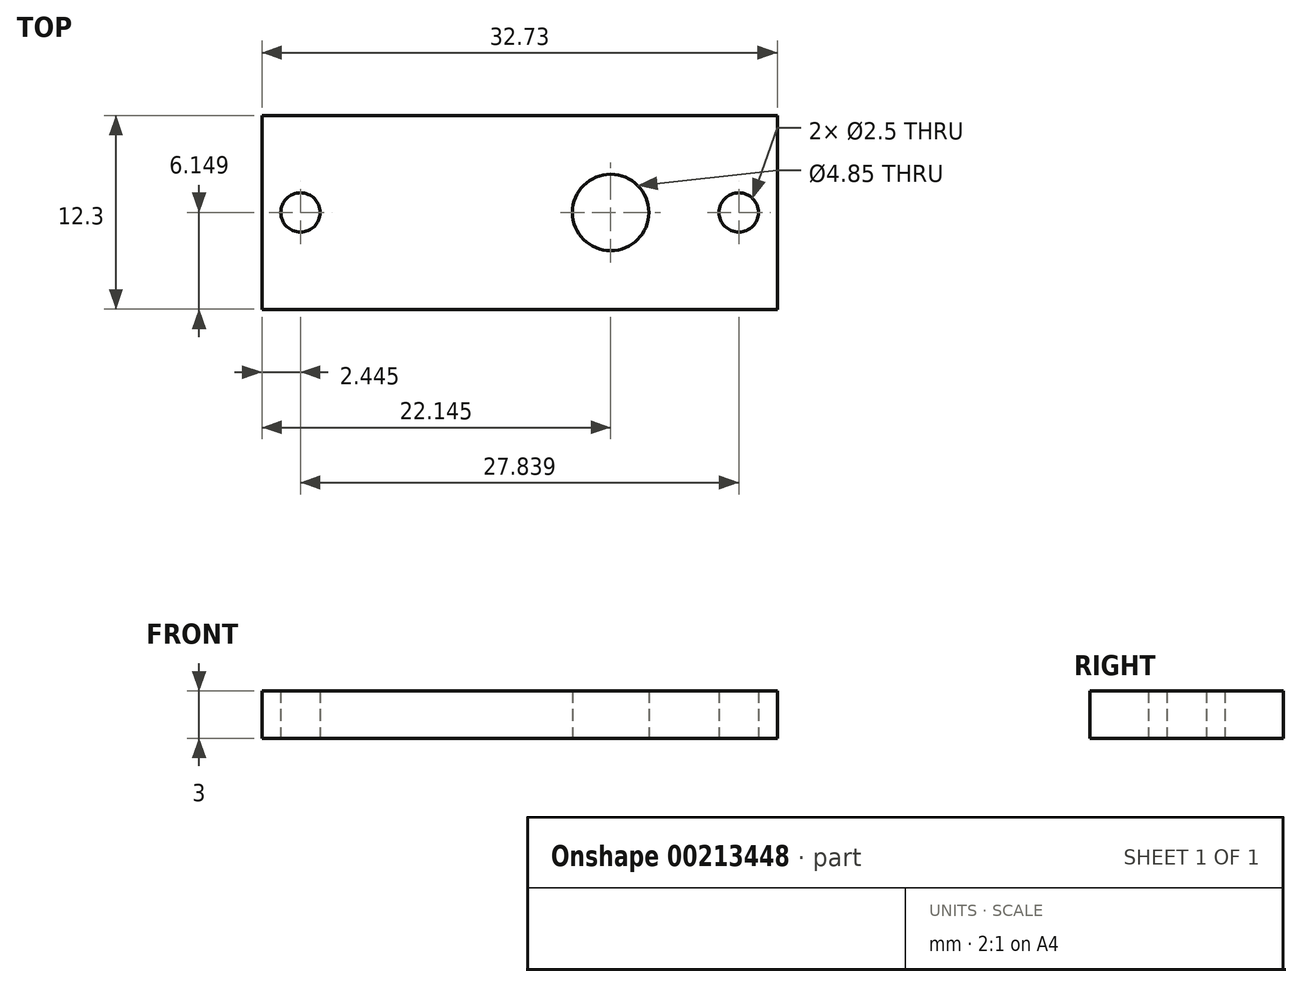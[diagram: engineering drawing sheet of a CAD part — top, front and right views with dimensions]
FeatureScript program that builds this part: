
annotation { "Feature Type Name" : "Feature", "Feature Type Description" : "" }
export const myFeature = defineFeature(function(context is Context, id is Id, definition is map)
    precondition{}
    {
        {
            var Q0;
            Q0=qCreatedBy(makeId("Top.planeOp"),FACE);
            var sketch = newSketch(context, id + "F0", { "sketchPlane" : qUnion([Q0])});
            skLineSegment(sketch, "E0.bottom", {"start": v(-20.9, 5.44) * mm, "end": v(11.82, 5.44) * mm});
            skLineSegment(sketch, "E0.top", {"start": v(-20.9, -6.86) * mm, "end": v(11.82, -6.86) * mm});
            skLineSegment(sketch, "E0.left", {"start": v(-20.9, 5.44) * mm, "end": v(-20.9, -6.86) * mm});
            skLineSegment(sketch, "E0.right", {"start": v(11.82, 5.44) * mm, "end": v(11.82, -6.86) * mm});
            skCircle(sketch, "E1", {"center": v(-18.47, -0.71) * mm, "radius": 1.25 * mm});
            skPoint(sketch, "E1.centerSnap0", {"position": v(-20.9, -0.71) * mm});
            skCircle(sketch, "E2", {"center": v(9.37, -0.71) * mm, "radius": 1.25 * mm});
            skPoint(sketch, "E2.centerSnap0", {"position": v(11.82, -0.71) * mm});
            skCircle(sketch, "E3", {"center": v(1.24, -0.71) * mm, "radius": 2.43 * mm});
            skSolve(sketch);
        }
        {
            var Q0;
            Q0=makeQuery(id+"F0.imprint","IMPRINT",FACE,{"disambiguationData":[TD([[makeQuery(id+"F0.imprint","IMPRINT",EDGE,{"derivedFrom":sQuery(id+"F0.wireOp",EDGE,"E0.bottom")}),-1.0]])]});
            extrude(context, id + "F1", {"entities" : qUnion([Q0]), "depth" : 3 * mm});
        }
    });
